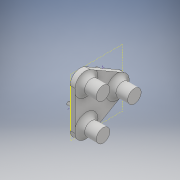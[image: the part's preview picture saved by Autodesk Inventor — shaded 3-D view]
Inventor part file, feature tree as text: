
AUTODESK INVENTOR PART (.ipt)
format: ipt  version: 2018 (Build 220112000, 112)  size: 351,744 bytes
history: native  units: mm
features: sketch x8, extrude x6, fillet x2, other x1
ambient origin geometry x8: Origin, YZ Plane, XZ Plane, XY Plane, X Axis, Y Axis, Z Axis, Center Point
bodies: Solid1 (feature_tree)
feature tree (17):
  extrude  "Extrusion1"  Depth=1.5mm TaperAngle=0.0deg
  fillet  "Fillet1"  Radius=3.0mm
  sketch  "Sketch2"  dims[d126=1.0mm d127=1.0mm]
  sketch  "Sketch3"  dims[d128=1.0mm d129=1.5mm d130=0.0mm]
  extrude  "Extrusion2"  Depth=1.0mm
  extrude  "Extrusion3"  Depth=1.5mm TaperAngle=0.0deg
  extrude  "Extrusion4"  Depth=2.0mm
  extrude  "Extrusion5"  Depth=2.0mm TaperAngle=0.0deg
  extrude  "Extrusion6"  Depth=4.0mm
  fillet  "Fillet2"  Radius=4.0mm
  sketch  "Sketch1"  dims[d0=12.7mm d1=1.5mm d2=0.0mm d3=3.0mm]
  other  "Image2"
  sketch  "Sketch4"  dims[d132=2.0mm d133=2.0mm]
  sketch  "Sketch5"  dims[d134=2.0mm d135=3.0mm d136=0.0mm]
  sketch  "Sketch6"  dims[d137=4.0mm d138=4.0mm d139=4.0mm]
  sketch  "Sketch7"  dims[d140=3.0mm d141=0.0mm]
  sketch  "Sketch8"  dims[d142=4.0mm d143=2.0mm d144=0.0mm d145=4.0mm d146=2.0mm d147=0.0mm d148=1.5mm]
